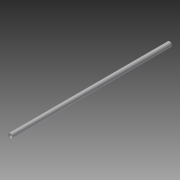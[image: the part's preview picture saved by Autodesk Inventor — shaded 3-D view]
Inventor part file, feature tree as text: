
AUTODESK INVENTOR PART (.ipt)
format: ipt  version: 2013 (Build 170138000, 138)  size: 69,120 bytes
history: native  units: in
note: dims shown in document units (in); Inventor stores cm internally (conversion verified against a paired STEP export)
features: extrude x1, sketch x1
ambient origin geometry x8: Origin, YZ Plane, XZ Plane, XY Plane, X Axis, Y Axis, Z Axis, Center Point
bodies: Solid1 (feature_tree)
feature tree (2):
  extrude  "Extrusion1"  Depth=1.33in
  sketch  "Sketch1"  dims[d0=1.5in d2=1.33in d3=51.13in d4=0.0in]
